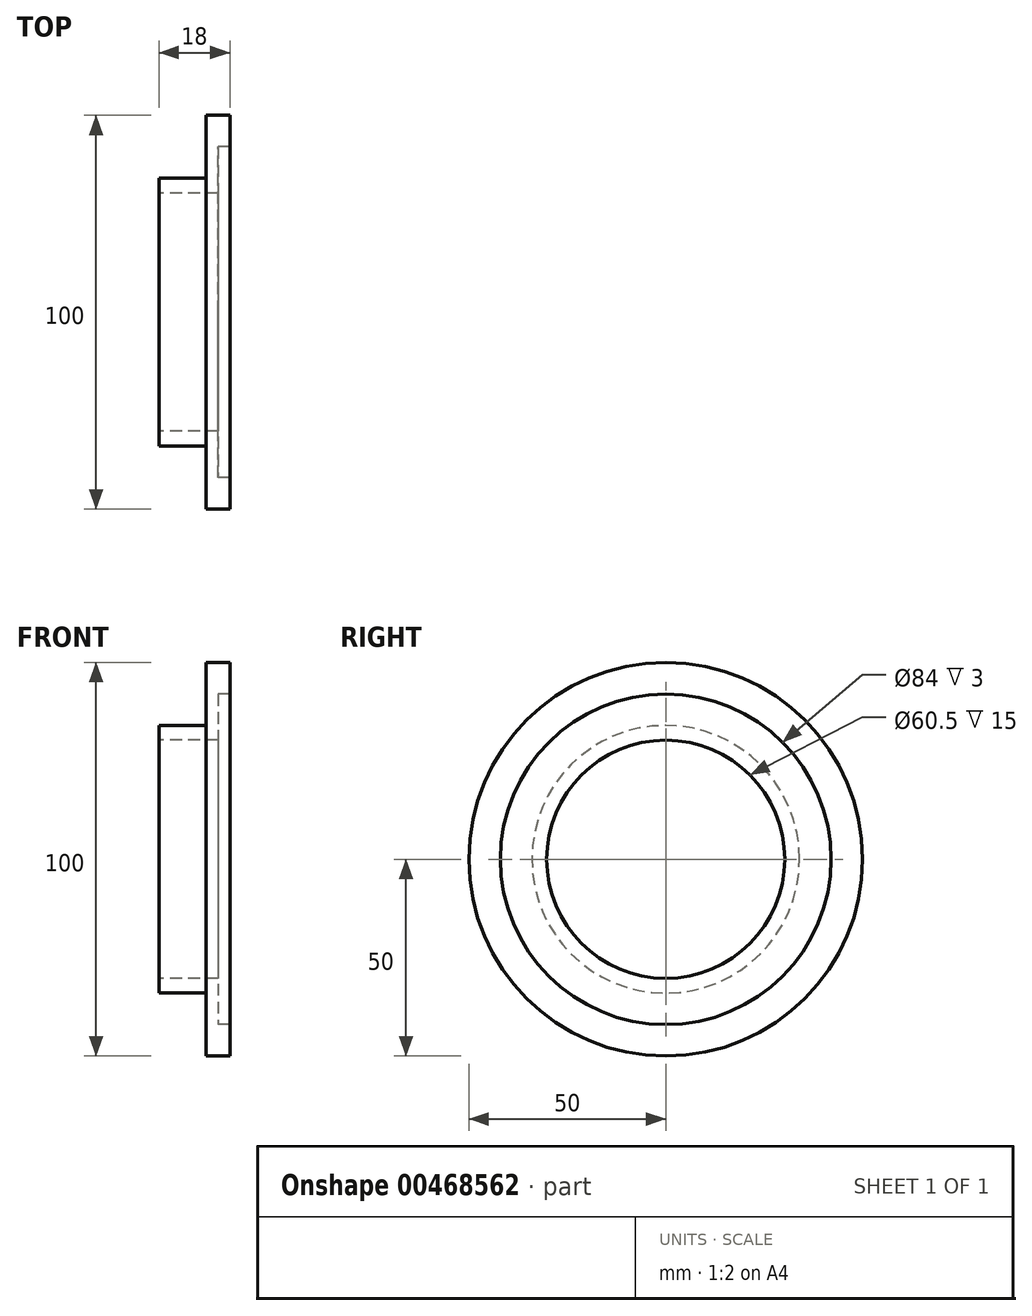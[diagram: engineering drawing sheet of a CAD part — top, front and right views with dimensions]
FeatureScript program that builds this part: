
annotation { "Feature Type Name" : "Feature", "Feature Type Description" : "" }
export const myFeature = defineFeature(function(context is Context, id is Id, definition is map)
    precondition{}
    {
        {
            var Q0;
            Q0=qCreatedBy(makeId("Front.planeOp"),FACE);
            var sketch = newSketch(context, id + "F0", { "sketchPlane" : qUnion([Q0])});
            skLineSegment(sketch, "E0", {"start": v(0, 0) * mm, "end": v(18, 0) * mm});
            skLineSegment(sketch, "E1", {"start": v(18, 0) * mm, "end": v(18, 50) * mm});
            skLineSegment(sketch, "E2", {"start": v(18, 50) * mm, "end": v(12, 50) * mm});
            skLineSegment(sketch, "E3", {"start": v(12, 50) * mm, "end": v(12, 34) * mm});
            skLineSegment(sketch, "E4", {"start": v(12, 34) * mm, "end": v(0, 34) * mm});
            skLineSegment(sketch, "E5", {"start": v(0, 34) * mm, "end": v(0, 0) * mm});
            skLineSegment(sketch, "E6", {"start": v(0, 30.25) * mm, "end": v(18, 30.25) * mm});
            skLineSegment(sketch, "E7", {"start": v(15, 50) * mm, "end": v(15, 0) * mm});
            skLineSegment(sketch, "E8", {"start": v(15, 42) * mm, "end": v(18, 42) * mm});
            skLineSegment(sketch, "E9", {"start": v(15, 5) * mm, "end": v(18, 5) * mm});
            skSolve(sketch);
        }
        {
            var Q0;
            {var subQ4=sQuery(id+"F0.wireOp",EDGE,"E3");Q0=makeQuery(id+"F0.imprint","IMPRINT",FACE,{"disambiguationData":[TD([[makeQuery(id+"F0.imprint","IMPRINT",EDGE,{"derivedFrom":subQ4}),1.0]])]});}
            var Q1;
            {var subQ3=sQuery(id+"F0.wireOp",EDGE,"E8");Q1=makeQuery(id+"F0.imprint","IMPRINT",FACE,{"disambiguationData":[TD([[makeQuery(id+"F0.imprint","IMPRINT",EDGE,{"derivedFrom":subQ3}),1.0]])]});}
            var Q2;
            Q2=sQuery(id+"F0.wireOp",EDGE,"E0");
            revolve(context, id + "F1", {"surfaceOperationType" : NewSurfaceOperationType.NEW, "entities" : qUnion([Q0, Q1]), "axis" : qUnion([Q2]), "revolveType" : RevolveType.FULL});
        }
    });
